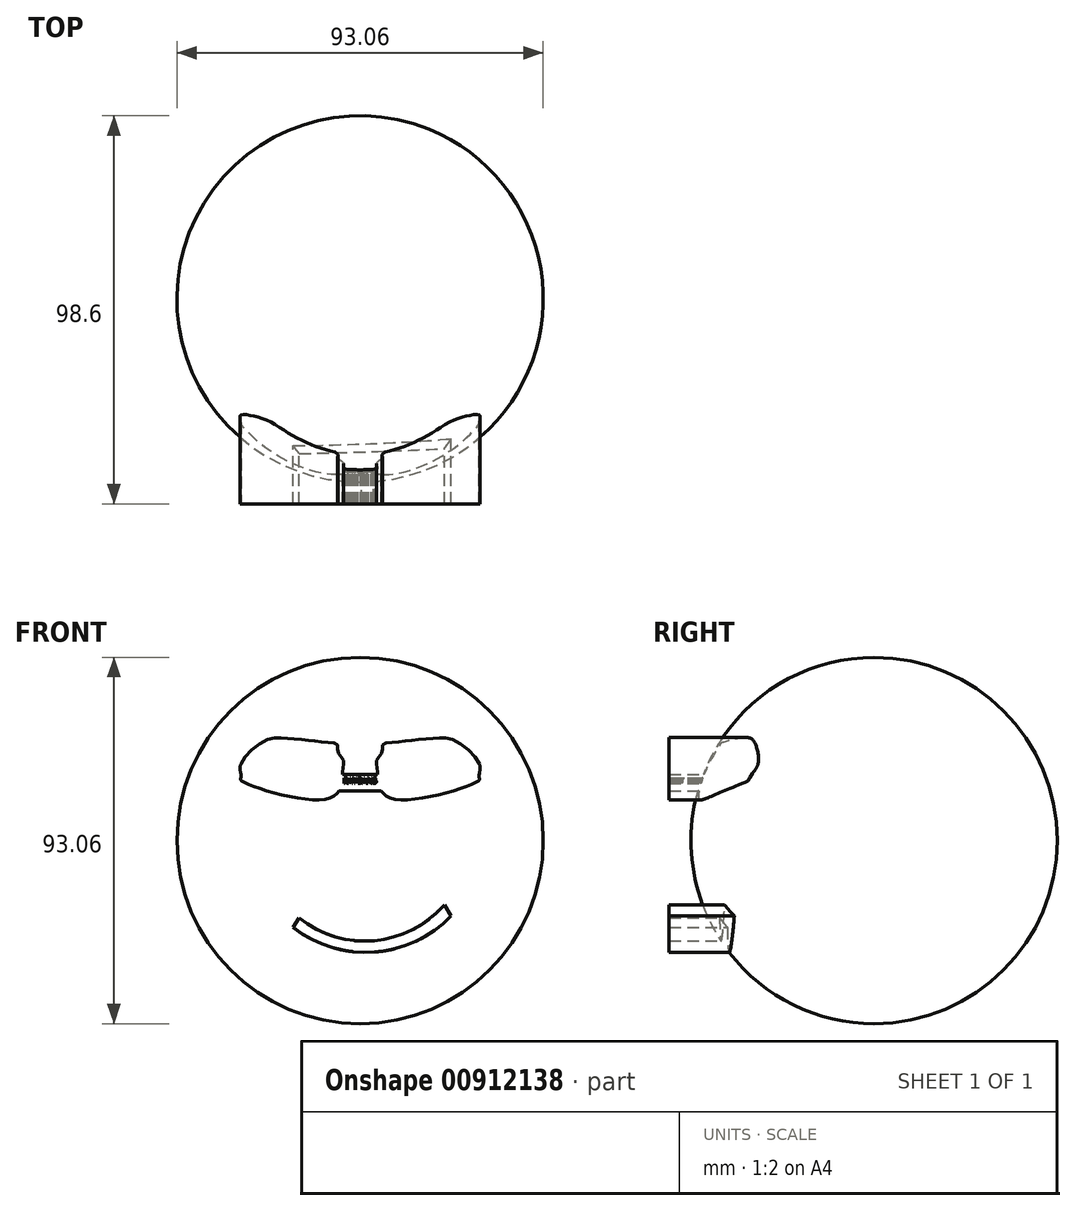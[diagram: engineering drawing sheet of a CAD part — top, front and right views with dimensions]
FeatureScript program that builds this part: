
annotation { "Feature Type Name" : "Feature", "Feature Type Description" : "" }
export const myFeature = defineFeature(function(context is Context, id is Id, definition is map)
    precondition{}
    {
        {
            var Q0;
            Q0=qCreatedBy(makeId("Front.planeOp"),FACE);
            var sketch = newSketch(context, id + "F0", { "sketchPlane" : qUnion([Q0])});
            skArc(sketch, "E0", {"start": v(0, -46.53) * mm, "mid": v(46.53, 0) * mm, "end": v(0, 46.53) * mm});
            skLineSegment(sketch, "E1", {"start": v(0, 46.53) * mm, "end": v(0, -46.53) * mm});
            skSolve(sketch);
        }
        {
            var Q0;
            Q0=makeQuery(id+"F0.imprint","IMPRINT",FACE,{"disambiguationData":[TD([[makeQuery(id+"F0.imprint","IMPRINT",EDGE,{"derivedFrom":sQuery(id+"F0.wireOp",EDGE,"E0")}),1.0]])]});
            var Q1;
            Q1=sQuery(id+"F0.wireOp",EDGE,"E1");
            revolve(context, id + "F1", {"surfaceOperationType" : NewSurfaceOperationType.NEW, "entities" : qUnion([Q0]), "axis" : qUnion([Q1]), "revolveType" : RevolveType.FULL});
        }
        {
            var Q0;
            Q0=qCreatedBy(makeId("Front.planeOp"),FACE);
            var sketch = newSketch(context, id + "F2", { "sketchPlane" : qUnion([Q0])});
            skLineSegment(sketch, "E2", {"start": v(-42.5, 19.5) * mm, "end": v(-30.29, 19.5) * mm});
            skLineSegment(sketch, "E3", {"start": v(-43.56, 17) * mm, "end": v(-30.29, 17) * mm});
            skFitSpline(sketch, "E4", {"points": [v(-30.29, 19.5) * mm, v(-23.77, 25.54) * mm, v(-18.9, 26.02) * mm, v(-13.57, 25.54) * mm, v(-8.83, 24.95) * mm, v(-5.75, 24.36) * mm, v(-5.63, 22.58) * mm, v(-4.33, 20.56) * mm, v(-4.2, 19.5) * mm, v(-4.45, 17.72) * mm, v(-4.45, 16.77) * mm, v(-4.56, 15.59) * mm, v(-7.76, 10.73) * mm, v(-30.29, 15.35) * mm, v(-30.29, 15.94) * mm, v(-30.29, 17) * mm, v(-30.29, 19.5) * mm]});
            skLineSegment(sketch, "E5", {"start": v(-4.45, 16.77) * mm, "end": v(0, 16.77) * mm});
            skLineSegment(sketch, "E6.MirrorCS", {"start": v(42.5, 19.5) * mm, "end": v(30.29, 19.5) * mm});
            skLineSegment(sketch, "E7.MirrorCS", {"start": v(43.56, 17) * mm, "end": v(30.29, 17) * mm});
            skFitSpline(sketch, "E8.MirrorC", {"points": [v(30.29, 19.5) * mm, v(23.77, 25.54) * mm, v(18.9, 26.02) * mm, v(13.57, 25.54) * mm, v(8.83, 24.95) * mm, v(5.75, 24.36) * mm, v(5.63, 22.58) * mm, v(4.33, 20.56) * mm, v(4.2, 19.5) * mm, v(4.45, 17.72) * mm, v(4.45, 16.77) * mm, v(4.56, 15.59) * mm, v(7.76, 10.73) * mm, v(30.29, 15.35) * mm, v(30.29, 15.94) * mm, v(30.29, 17) * mm, v(30.29, 19.5) * mm]});
            skLineSegment(sketch, "E9.MirrorCS", {"start": v(4.45, 16.77) * mm, "end": v(0, 16.77) * mm});
            skLineSegment(sketch, "E10", {"start": v(-5.37, 12.64) * mm, "end": v(5.37, 12.64) * mm});
            skText(sketch, "E11", { "text": "RAYBANS", "fontName": "OpenSans-Regular.ttf"});
            skArc(sketch, "E12", {"start": v(-17.02, -22.08) * mm, "mid": v(3.62, -28.33) * mm, "end": v(23.16, -19.19) * mm});
            skArc(sketch, "E13", {"start": v(-15.47, -19.6) * mm, "mid": v(3.64, -25.45) * mm, "end": v(21.4, -16.3) * mm});
            skLineSegment(sketch, "E14", {"start": v(-15.47, -19.6) * mm, "end": v(-17.02, -22.08) * mm});
            skLineSegment(sketch, "E15", {"start": v(21.4, -16.3) * mm, "end": v(23.16, -19.19) * mm});
            skLineSegment(sketch, "E16", {"start": v(-19.13, -24.54) * mm, "end": v(-13.99, -17.42) * mm});
            skLineSegment(sketch, "E17", {"start": v(25.48, -21.58) * mm, "end": v(19.56, -14.25) * mm});
            skFitSpline(sketch, "E18", {"points": [v(-36.49, 29.26) * mm, v(-35.15, 40.4) * mm, v(-33.47, 34.46) * mm, v(-33.13, 33.28) * mm, v(-32.38, 40.5) * mm, v(-29.87, 35.71) * mm, v(-29.87, 41.91) * mm, v(-27.6, 37.9) * mm, v(-28.44, 43.5) * mm, v(-26.01, 38.4) * mm, v(-27.18, 44.6) * mm, v(-23.16, 40.4) * mm, v(-24.59, 45.77) * mm, v(-20.65, 41.66) * mm, v(-22.15, 46.27) * mm, v(-17.71, 42.84) * mm, v(-19.47, 47.45) * mm, v(-16.37, 43.6) * mm, v(-17.3, 48.03) * mm, v(-14.53, 44.35) * mm, v(-14.7, 48.54) * mm, v(-12.1, 44.68) * mm, v(-13.02, 49.46) * mm, v(-10.84, 45.35) * mm, v(-10.42, 49.37) * mm, v(-9.33, 45.69) * mm, v(-8.91, 51.05) * mm, v(-7.4, 46.1) * mm, v(-6.9, 51.55) * mm, v(-5.4, 46.1) * mm, v(-5.22, 51.72) * mm, v(-3.46, 46.7) * mm, v(-2.88, 51.89) * mm, v(-0.7, 46.36) * mm, v(0, 51.55) * mm, v(1.31, 46.86) * mm, v(2.49, 52.06) * mm, v(2.82, 46.19) * mm, v(4.83, 51.22) * mm, v(5.5, 46.36) * mm, v(6.68, 47.36) * mm, v(7.94, 50.13) * mm, v(8.86, 46.6) * mm, v(8.77, 45.85) * mm, v(10.62, 48.45) * mm, v(10.7, 44.85) * mm, v(12.04, 48.28) * mm, v(13.05, 44.85) * mm, v(15.98, 47.36) * mm, v(15.14, 44.01) * mm, v(19.33, 45.94) * mm, v(19.59, 42.33) * mm, v(22.18, 46.19) * mm, v(21.35, 41.33) * mm, v(26.3, 45.1) * mm, v(25.87, 38.48) * mm, v(30.48, 43.42) * mm, v(29.06, 36.3) * mm, v(29.73, 36.3) * mm], "startDerivative": vector(35.4, 649.16) * mm, "endDerivative": vector(138.9, 70.86) * mm});
            skLineSegment(sketch, "E19", {"start": v(0, 0) * mm, "end": v(66.77, 0) * mm});
            skLineSegment(sketch, "E20", {"start": v(-0.2, -3.65) * mm, "end": v(67.9, -2.94) * mm});
            skArc(sketch, "E21", {"start": v(68.08, -2.88) * mm, "mid": v(68.44, -1.02) * mm, "end": v(66.95, 0.14) * mm});
            skLineSegment(sketch, "E22", {"start": v(67.91, -2.92) * mm, "end": v(68.1, -2.9) * mm});
            skLineSegment(sketch, "E23", {"start": v(66.93, 0.06) * mm, "end": v(66.73, 0) * mm});
            skLineSegment(sketch, "E24", {"start": v(66.93, 0.06) * mm, "end": v(66.96, 0.14) * mm});
            const initialGuessF2  = {"E11": [-0.00428, 0.01454, 1, 0, 0.0014]};
            skSetInitialGuess(sketch, initialGuessF2);
            skSolve(sketch);
        }
        {
            var Q0;
            Q0 = qSketchRegion(id + "F2", true);
            extrude(context, id + "F3", {"entities" : qUnion([Q0]), "operationType" : NewBodyOperationType.ADD, "depth" : 52.07 * mm, "offsetDistance" : 25.4 * mm});
        }
    });
